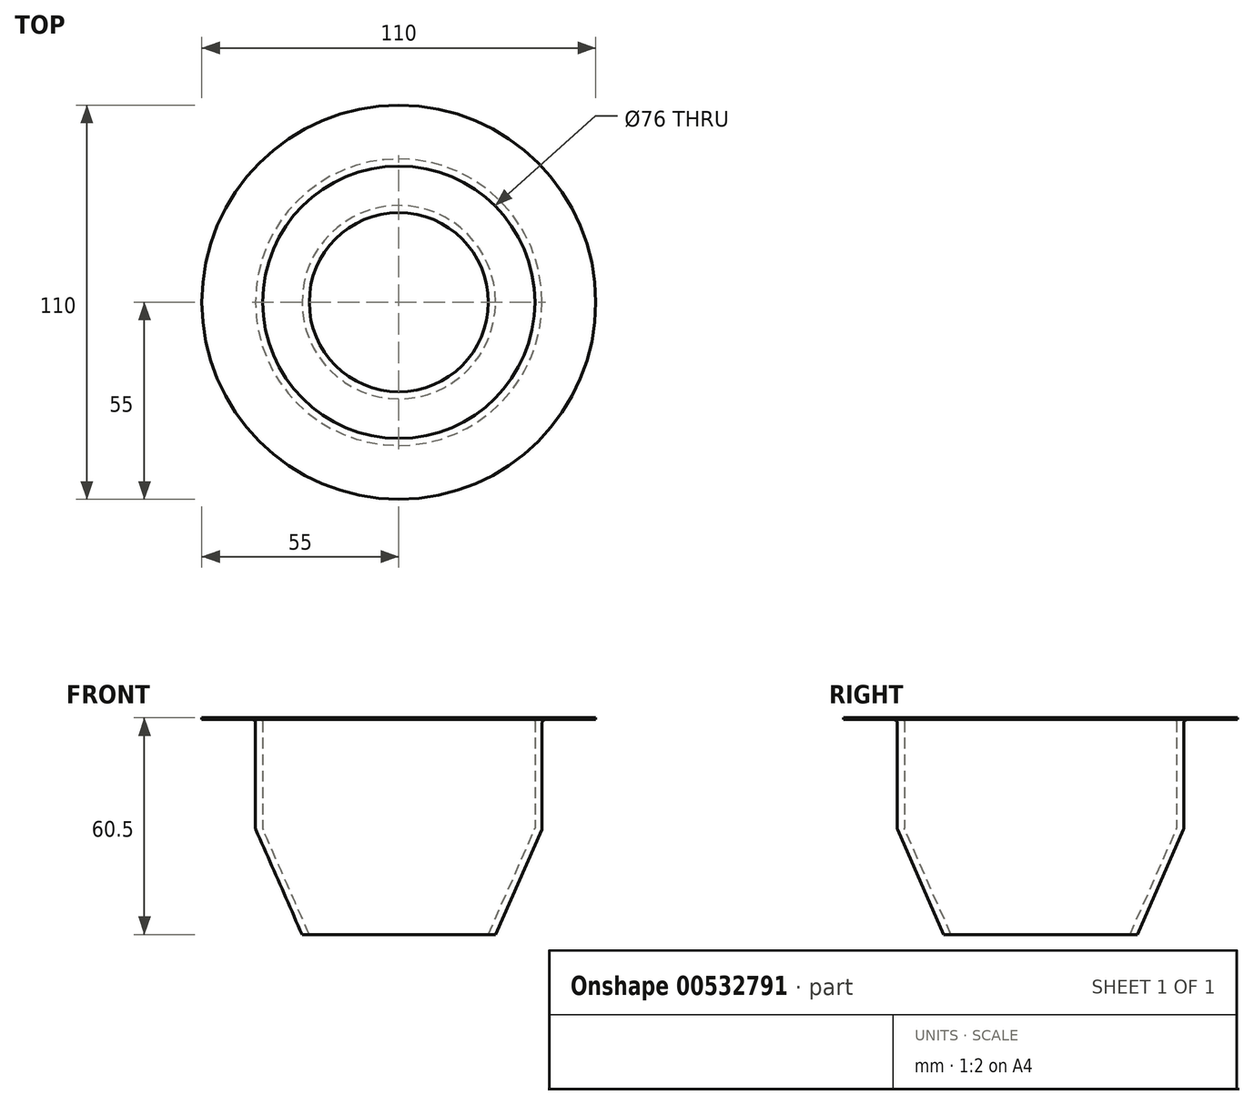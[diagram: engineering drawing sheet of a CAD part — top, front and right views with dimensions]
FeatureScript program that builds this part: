
annotation { "Feature Type Name" : "Feature", "Feature Type Description" : "" }
export const myFeature = defineFeature(function(context is Context, id is Id, definition is map)
    precondition{}
    {
        {
            var Q0;
            Q0=qCreatedBy(makeId("Front.planeOp"),FACE);
            var sketch = newSketch(context, id + "F0", { "sketchPlane" : qUnion([Q0])});
            skLineSegment(sketch, "E0", {"start": v(0, 0) * mm, "end": v(0, 39.05) * mm});
            skLineSegment(sketch, "E1", {"start": v(-41, 60) * mm, "end": v(-55, 60) * mm});
            skLineSegment(sketch, "E2", {"start": v(-55, 60) * mm, "end": v(-55, 60.5) * mm});
            skLineSegment(sketch, "E3", {"start": v(-39, 60.5) * mm, "end": v(-55, 60.5) * mm});
            skPoint(sketch, "E4.visualSharp", {"position": v(-40, 60) * mm});
            skArc(sketch, "E4.filletArc", {"start": v(-40, 59) * mm, "mid": v(-40.3, 59.7) * mm, "end": v(-41, 60) * mm});
            skPoint(sketch, "E5.visualSharp", {"position": v(-38, 60.5) * mm});
            skArc(sketch, "E5.filletArc", {"start": v(-38, 59.5) * mm, "mid": v(-38.3, 60.2) * mm, "end": v(-39, 60.5) * mm});
            skLineSegment(sketch, "E6", {"start": v(-38, 59.5) * mm, "end": v(-38, 29.71) * mm});
            skLineSegment(sketch, "E7", {"start": v(-37.92, 29.3) * mm, "end": v(-25, 0) * mm});
            skLineSegment(sketch, "E8", {"start": v(-40, 59) * mm, "end": v(-40, 29.71) * mm});
            skLineSegment(sketch, "E9", {"start": v(-39.92, 29.3) * mm, "end": v(-27, 0) * mm});
            skLineSegment(sketch, "E10", {"start": v(-27, 0) * mm, "end": v(-25, 0) * mm});
            skPoint(sketch, "E11.visualSharp", {"position": v(-40, 29.5) * mm});
            skArc(sketch, "E11.filletArc", {"start": v(-40, 29.71) * mm, "mid": v(-39.98, 29.5) * mm, "end": v(-39.92, 29.3) * mm});
            skPoint(sketch, "E12.visualSharp", {"position": v(-38, 29.5) * mm});
            skArc(sketch, "E12.filletArc", {"start": v(-38, 29.71) * mm, "mid": v(-37.98, 29.5) * mm, "end": v(-37.92, 29.3) * mm});
            skSolve(sketch);
        }
        {
            var Q0;
            Q0=makeQuery(id+"F0.imprint","IMPRINT",FACE,{"disambiguationData":[TD([[makeQuery(id+"F0.imprint","IMPRINT",EDGE,{"derivedFrom":sQuery(id+"F0.wireOp",EDGE,"QkPvC10W-7wmO-x4D7-Ebhb-pvV664LUZhOL")}),-1.0]])]});
            var Q1;
            Q1=makeQuery(id+"F0.imprint","IMPRINT",FACE,{"disambiguationData":[TD([[makeQuery(id+"F0.imprint","IMPRINT",EDGE,{"derivedFrom":sQuery(id+"F0.wireOp",EDGE,"E1")}),-1.0]])]});
            var Q2;
            Q2=sQuery(id+"F0.wireOp",EDGE,"E0");
            revolve(context, id + "F1", {"entities" : qUnion([Q0, Q1]), "axis" : qUnion([Q2]), "revolveType" : RevolveType.FULL});
        }
    });
